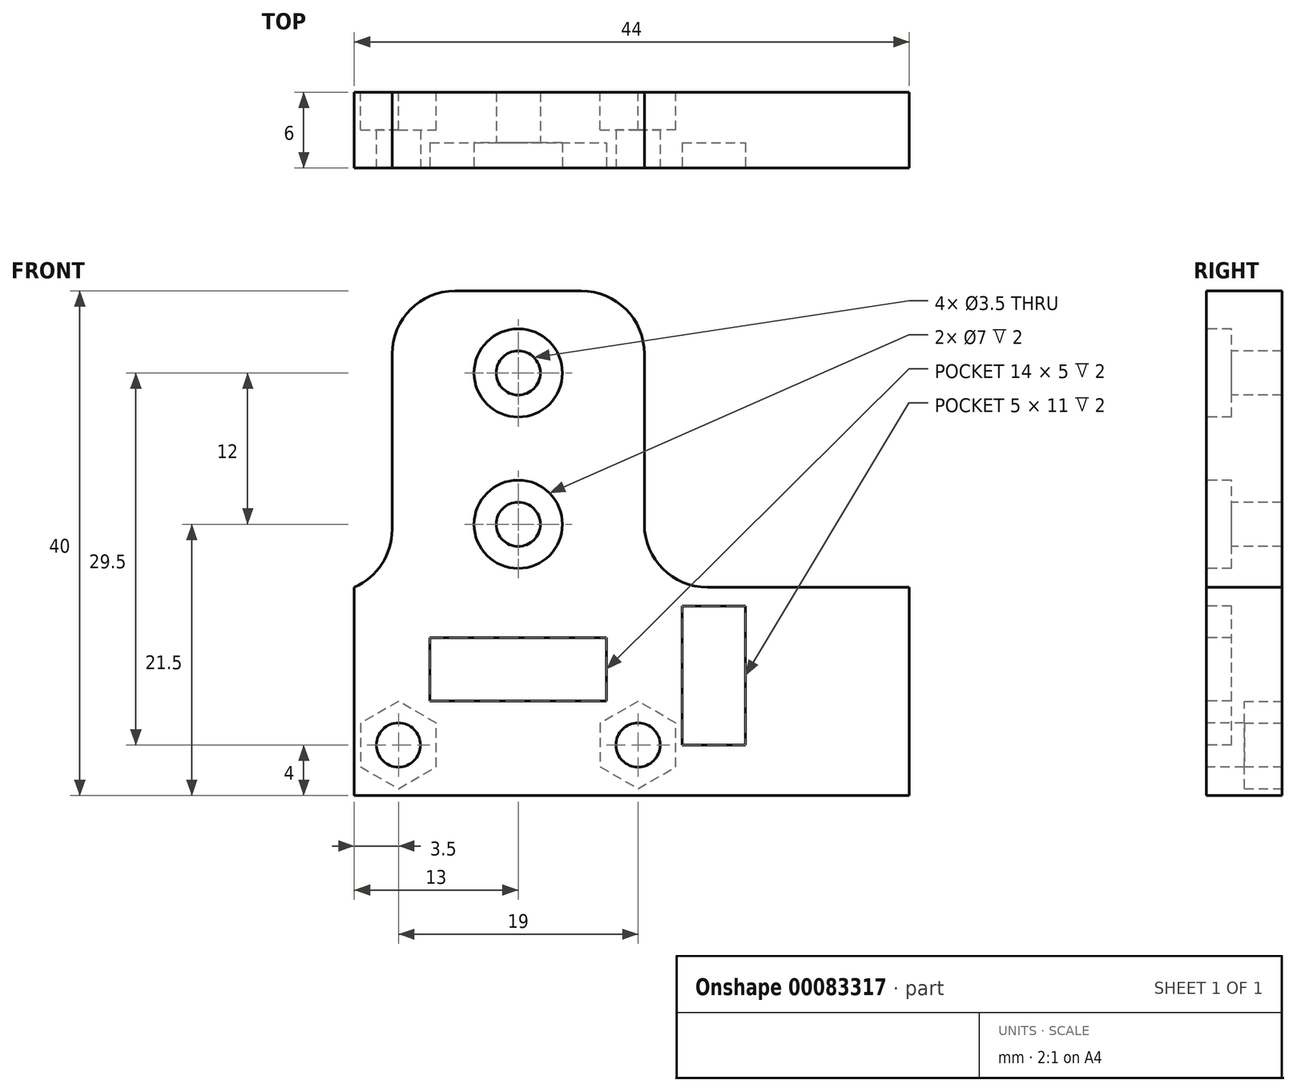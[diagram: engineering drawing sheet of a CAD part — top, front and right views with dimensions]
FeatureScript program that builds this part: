
annotation { "Feature Type Name" : "Feature", "Feature Type Description" : "" }
export const myFeature = defineFeature(function(context is Context, id is Id, definition is map)
    precondition{}
    {
        {
            var Q0;
            Q0=qCreatedBy(makeId("Front.planeOp"),FACE);
            var sketch = newSketch(context, id + "F0", { "sketchPlane" : qUnion([Q0])});
            skLineSegment(sketch, "E0.top", {"start": v(32.5, -20) * mm, "end": v(-11.5, -20) * mm});
            skPoint(sketch, "E0.middle", {"position": v(0, 0) * mm});
            skLineSegment(sketch, "E1", {"start": v(-11.5, -18.5) * mm, "end": v(32.5, -18.5) * mm, "construction": true});
            skLineSegment(sketch, "E2", {"start": v(-11.5, -16) * mm, "end": v(32.5, -16) * mm, "construction": true});
            skCircle(sketch, "E3", {"center": v(-8, -16) * mm, "radius": 1.75 * mm});
            skCircle(sketch, "E4", {"center": v(11, -16) * mm, "radius": 1.75 * mm});
            skLineSegment(sketch, "E5.bottom", {"start": v(14.5, -16) * mm, "end": v(19.5, -16) * mm});
            skLineSegment(sketch, "E5.top", {"start": v(14.5, -5) * mm, "end": v(19.5, -5) * mm});
            skLineSegment(sketch, "E5.left", {"start": v(14.5, -16) * mm, "end": v(14.5, -5) * mm});
            skLineSegment(sketch, "E5.right", {"start": v(19.5, -16) * mm, "end": v(19.5, -5) * mm});
            skLineSegment(sketch, "E6.bottom", {"start": v(-5.5, -12.5) * mm, "end": v(8.5, -12.5) * mm});
            skLineSegment(sketch, "E6.top", {"start": v(-5.5, -7.5) * mm, "end": v(8.5, -7.5) * mm});
            skLineSegment(sketch, "E6.left", {"start": v(-5.5, -12.5) * mm, "end": v(-5.5, -7.5) * mm});
            skLineSegment(sketch, "E6.right", {"start": v(8.5, -12.5) * mm, "end": v(8.5, -7.5) * mm});
            skCircle(sketch, "E7", {"center": v(1.5, 13.5) * mm, "radius": 1.75 * mm});
            skCircle(sketch, "E8", {"center": v(1.5, 1.5) * mm, "radius": 1.75 * mm});
            skCircle(sketch, "E9", {"center": v(1.5, 13.5) * mm, "radius": 3.5 * mm});
            skCircle(sketch, "E10", {"center": v(1.5, 1.5) * mm, "radius": 3.5 * mm});
            skLineSegment(sketch, "E11", {"start": v(-11.5, -20) * mm, "end": v(-11.5, -3.5) * mm});
            skLineSegment(sketch, "E12", {"start": v(-11.5, -3.5) * mm, "end": v(-8.5, -3.5) * mm});
            skLineSegment(sketch, "E13", {"start": v(-8.5, -3.5) * mm, "end": v(-8.5, 20) * mm});
            skLineSegment(sketch, "E14", {"start": v(-8.5, 20) * mm, "end": v(11.5, 20) * mm});
            skLineSegment(sketch, "E15", {"start": v(11.5, 20) * mm, "end": v(11.5, -3.5) * mm});
            skLineSegment(sketch, "E16", {"start": v(11.5, -3.5) * mm, "end": v(32.5, -3.5) * mm});
            skLineSegment(sketch, "E17", {"start": v(32.5, -3.5) * mm, "end": v(32.5, -20) * mm});
            skSolve(sketch);
        }
        {
            var Q0;
            Q0=makeQuery(id+"F0.imprint","IMPRINT",FACE,{"disambiguationData":[TD([[makeQuery(id+"F0.imprint","IMPRINT",EDGE,{"derivedFrom":sQuery(id+"F0.wireOp",EDGE,"E0.top")}),-1.0]])]});
            var Q1;
            Q1=makeQuery(id+"F0.imprint","IMPRINT",FACE,{"disambiguationData":[TD([[makeQuery(id+"F0.imprint","IMPRINT",EDGE,{"derivedFrom":sQuery(id+"F0.wireOp",EDGE,"E6.bottom")}),1.0]])]});
            var Q2;
            Q2=makeQuery(id+"F0.imprint","IMPRINT",FACE,{"disambiguationData":[TD([[makeQuery(id+"F0.imprint","IMPRINT",EDGE,{"derivedFrom":sQuery(id+"F0.wireOp",EDGE,"E5.bottom")}),1.0]])]});
            var Q3;
            Q3=makeQuery(id+"F0.imprint","IMPRINT",FACE,{"disambiguationData":[TD([[makeQuery(id+"F0.imprint","IMPRINT",EDGE,{"derivedFrom":sQuery(id+"F0.wireOp",EDGE,"E8")}),-1.0]])]});
            var Q4;
            Q4=makeQuery(id+"F0.imprint","IMPRINT",FACE,{"disambiguationData":[TD([[makeQuery(id+"F0.imprint","IMPRINT",EDGE,{"derivedFrom":sQuery(id+"F0.wireOp",EDGE,"E7")}),-1.0]])]});
            extrude(context, id + "F1", {"entities" : qUnion([Q0, Q1, Q2, Q3, Q4]), "oppositeDirection" : true, "depth" : 6 * mm});
        }
        {
            var Q0;
            Q0=makeQuery(id+"F0.imprint","IMPRINT",FACE,{"disambiguationData":[TD([[makeQuery(id+"F0.imprint","IMPRINT",EDGE,{"derivedFrom":sQuery(id+"F0.wireOp",EDGE,"E5.bottom")}),1.0]])]});
            var Q1;
            Q1=makeQuery(id+"F0.imprint","IMPRINT",FACE,{"disambiguationData":[TD([[makeQuery(id+"F0.imprint","IMPRINT",EDGE,{"derivedFrom":sQuery(id+"F0.wireOp",EDGE,"E6.bottom")}),1.0]])]});
            var Q2;
            Q2=makeQuery(id+"F0.imprint","IMPRINT",FACE,{"disambiguationData":[TD([[makeQuery(id+"F0.imprint","IMPRINT",EDGE,{"derivedFrom":sQuery(id+"F0.wireOp",EDGE,"E7")}),-1.0]])]});
            var Q3;
            Q3=makeQuery(id+"F0.imprint","IMPRINT",FACE,{"disambiguationData":[TD([[makeQuery(id+"F0.imprint","IMPRINT",EDGE,{"derivedFrom":sQuery(id+"F0.wireOp",EDGE,"E8")}),-1.0]])]});
            extrude(context, id + "F2", {"entities" : qUnion([Q0, Q1, Q2, Q3]), "operationType" : NewBodyOperationType.REMOVE, "oppositeDirection" : true, "depth" : 2 * mm});
        }
        {
            var Q0;
            Q0=makeQuery(id+"F1.opExtrude","CAP_FACE",FACE,{"disambiguationData":[OSD([sQuery(id+"F0.wireOp",EDGE,"E0.top"),sQuery(id+"F0.wireOp",EDGE,"E0.left"),sQuery(id+"F0.wireOp",EDGE,"E3"),sQuery(id+"F0.wireOp",EDGE,"E4"),sQuery(id+"F0.wireOp",EDGE,"E7"),sQuery(id+"F0.wireOp",EDGE,"E8"),sQuery(id+"F0.wireOp",EDGE,"E11"),sQuery(id+"F0.wireOp",EDGE,"E12"),sQuery(id+"F0.wireOp",EDGE,"E13"),sQuery(id+"F0.wireOp",EDGE,"E14")])],"isStart":false});
            var sketch = newSketch(context, id + "F3", { "sketchPlane" : qUnion([Q0])});
            skCircle(sketch, "E18.cCircle", {"center": v(-11, -16) * mm, "radius": 3 * mm, "construction": true});
            skLineSegment(sketch, "E18.0", {"start": v(-14, -14.27) * mm, "end": v(-11, -12.54) * mm});
            skLineSegment(sketch, "E18.1", {"start": v(-11, -12.54) * mm, "end": v(-8, -14.27) * mm});
            skLineSegment(sketch, "E18.2", {"start": v(-8, -14.27) * mm, "end": v(-8, -17.73) * mm});
            skLineSegment(sketch, "E18.3", {"start": v(-8, -17.73) * mm, "end": v(-11, -19.46) * mm});
            skLineSegment(sketch, "E18.4", {"start": v(-11, -19.46) * mm, "end": v(-14, -17.73) * mm});
            skLineSegment(sketch, "E18.5", {"start": v(-14, -17.73) * mm, "end": v(-14, -14.27) * mm});
            skPoint(sketch, "E18.0.midPoint", {"position": v(-12.5, -13.4) * mm});
            skCircle(sketch, "E19.cCircle", {"center": v(8, -16) * mm, "radius": 3 * mm, "construction": true});
            skLineSegment(sketch, "E19.0", {"start": v(5, -17.73) * mm, "end": v(5, -14.27) * mm});
            skLineSegment(sketch, "E19.1", {"start": v(5, -14.27) * mm, "end": v(8, -12.54) * mm});
            skLineSegment(sketch, "E19.2", {"start": v(8, -12.54) * mm, "end": v(11, -14.27) * mm});
            skLineSegment(sketch, "E19.3", {"start": v(11, -14.27) * mm, "end": v(11, -17.73) * mm});
            skLineSegment(sketch, "E19.4", {"start": v(11, -17.73) * mm, "end": v(8, -19.46) * mm});
            skLineSegment(sketch, "E19.5", {"start": v(8, -19.46) * mm, "end": v(5, -17.73) * mm});
            skPoint(sketch, "E19.0.midPoint", {"position": v(5, -16) * mm});
            skSolve(sketch);
        }
        {
            var Q0;
            Q0=qSketchRegion(id+"F3",true);
            extrude(context, id + "F4", {"entities" : qUnion([Q0]), "operationType" : NewBodyOperationType.REMOVE, "oppositeDirection" : true, "depth" : 3 * mm});
        }
        {
            var Q0;
            Q0=makeQuery(id+"F1.opExtrude","SWEPT_EDGE",EDGE,{"disambiguationData":[OSD([sQuery(id+"F0.wireOp",EDGE,"E12"),sQuery(id+"F0.wireOp",EDGE,"E13")])]});
            var Q1;
            Q1=makeQuery(id+"F1.opExtrude","SWEPT_EDGE",EDGE,{"disambiguationData":[OSD([sQuery(id+"F0.wireOp",EDGE,"E13"),sQuery(id+"F0.wireOp",EDGE,"E14")])]});
            var Q2;
            Q2=makeQuery(id+"F1.opExtrude","SWEPT_EDGE",EDGE,{"disambiguationData":[OSD([sQuery(id+"F0.wireOp",EDGE,"E0.left"),sQuery(id+"F0.wireOp",EDGE,"E14")])]});
            var Q3;
            Q3=makeQuery(id+"F1.opExtrude","SWEPT_EDGE",EDGE,{"disambiguationData":[OSD([sQuery(id+"F0.wireOp",EDGE,"E15"),sQuery(id+"F0.wireOp",EDGE,"E16")])]});
            fillet(context, id + "F5", {"entities" : qUnion([Q0, Q1, Q2, Q3]), "radius" : 5 * mm, "tangentPropagation" : true, "allowEdgeOverflow" : false});
        }
    });
